# Revit family: Sink-Vessel-Lavatory-KOHLER-Veil_Tall-K-20703-1
name_source: partatom
category: Plumbing Fixtures
units: mm (PartAtom-declared; Revit-internal decimal feet)

## family parameters
Cut with Voids When Loaded = No
Host = Face
OmniClass Number = 23.31.13.00
OmniClass Title = Sinks
Part Type = Normal
Room Calculation Point = No
Round Connector Dimension = Use Diameter
Shared = No

## types (6) — shared parameters
ADA Compliant = No
Assembly Code = D2010400
CW Connection = No
Cold Water Inlet = Cold Water Inlet
Date Modified = 09/12/2024
Default Elevation = 36"
Drain Included = No
HW Connection = No
Height = 15 1/16"
Hot Water Inlet = Hot Water Inlet
Length = 16"
Manufacturer = Kohler Co.
Master Format 2014 = 22 41 16
Master Format 2014 Name = Residential Lavatories and Sinks
Material = Fireclay
Product Documentation Link = https://www.us.kohler.com
Product Name = Veil Tall
Product Page URL = http://www.us.kohler.com
URL = https://www.us.kohler.com
Vent Connection = No
Waste Connection = Yes
Waste Water Outlet = Waste Water Outlet
WaterSense Certified = No
Width = 16"

## per-type parameters (varying)
| type | Description | Finish | Model | Type | With Overflow Drain | Without Overflow Drain |
| With Overflow Drain, 0-White | 16 Inch Round Vessel Bathroom Sink Or Pedestal Sink Basin | KOHLER-Fireclay-0-White | K-20703-0 | 1 | Yes | No |
| With Overflow Drain, 96-Biscuit | 16 Inch Round Vessel Bathroom Sink Or Pedestal Sink Basin | KOHLER-Fireclay-96-Biscuit | K-20703-96 | 3 | Yes | No |
| With Overflow Drain, 7-Black Black | 16 Inch Round Vessel Bathroom Sink Or Pedestal Sink Basin | KOHLER-Fireclay-7-Black_Black | K-20703-7 | 2 | Yes | No |
| Without Overflow Drain, 0-White | Pedestal Bathroom Sink Without Overflow | KOHLER-Fireclay-0-White | K-20703-N-0 | 4 | No | No |
| Without Overflow Drain, 96-Biscuit | Pedestal Bathroom Sink Without Overflow | KOHLER-Fireclay-96-Biscuit | K-20703-N-96 | 6 | No | Yes |
| Without Overflow Drain, 7-Black Black | Pedestal Bathroom Sink Without Overflow | KOHLER-Fireclay-7-Black_Black | K-20703-N-7 | 5 | No | Yes |

## geometry (parser evidence)
native form markers: Sweep x5
no freeform markers — native parametric forms only
